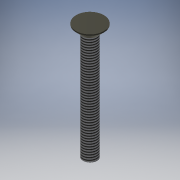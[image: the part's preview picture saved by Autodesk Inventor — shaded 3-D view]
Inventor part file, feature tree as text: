
AUTODESK INVENTOR PART (.ipt)
format: ipt  version: 2016 (Build 200138000, 138)  size: 131,072 bytes
history: native  units: mm
features: extrude x5, sketch x5, other x1, thread x1, chamfer x1
ambient origin geometry x1: Origin
bodies: Body1 (feature_tree)
feature tree (13):
  other  "ソリッド1"
  extrude  "押し出し1"  Depth=3.0mm
  extrude  "押し出し2"  Depth=6.0mm TaperAngle=0.0deg
  thread  "ねじ1"
  chamfer  "面取り1"  Distance=6.0mm
  extrude  "押し出し4"  Depth=1.75mm TaperAngle=0.0deg
  extrude  "押し出し5"  Depth=10.0mm TaperAngle=0.0deg
  extrude  "押し出し6"  Depth=1.5mm TaperAngle=45.0deg
  sketch  "スケッチ1"
  sketch  "スケッチ2"
  sketch  "スケッチ4"
  sketch  "スケッチ5"
  sketch  "スケッチ6"
